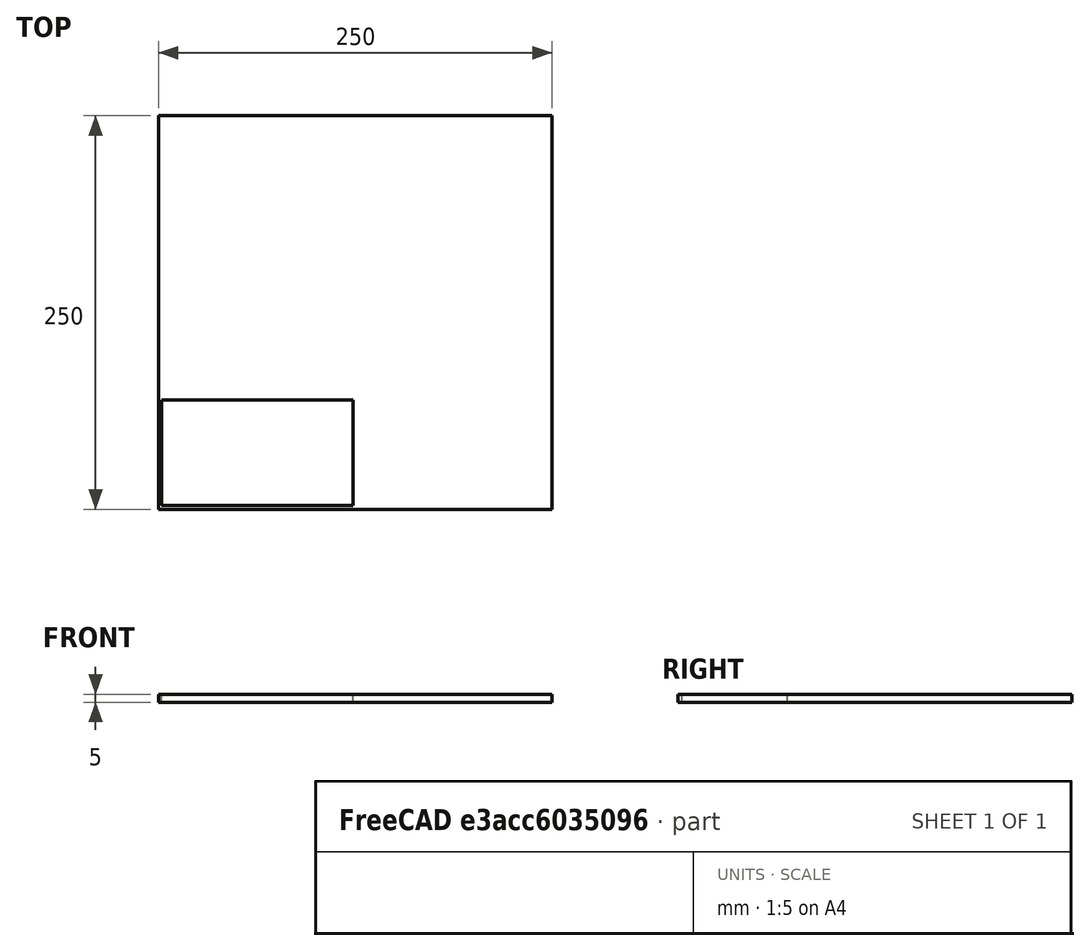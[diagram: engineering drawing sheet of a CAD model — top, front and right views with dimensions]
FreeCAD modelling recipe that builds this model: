
FCSTD DOCUMENT  (FreeCAD 0.18.4R)
Label: cnc
License: All rights reserved
LicenseURL: http://en.wikipedia.org/wiki/All_rights_reserved
objects: Path::FeaturePython×5, Part::FeaturePython×2, Part::Feature×1, App::FeaturePython×1, App::DocumentObjectGroup×1, Part::Box×1, Path::FeatureCompoundPython×1, Mesh::FeaturePython×1
note: 6 computed .brp shape members not serialized (recipe doc carries the construction recipe); baked Part::Feature solids carry a one-line shape summary decoded from their .brp

FEATURE [Part::Feature] Cut012035015003002009024006019011009006027002007011007005004011002017003001  label="drawbar001"
  Placement = pos=(163,44,-25.5) rot=(0,0,1;0rad)
  shape: bbox 119.5 x 65 x 5 mm, 31 faces (baked)
FEATURE [App::FeaturePython] SetupSheet  # Path/CAM operation (typed FeaturePython)
  ClearanceHeightExpression = OpStockZMax+SetupSheet.ClearanceHeightOffset
  ClearanceHeightOffset = 5
  FinalDepthExpression = OpFinalDepth
  HorizRapid = 15
  SafeHeightExpression = OpStockZMax+SetupSheet.SafeHeightOffset
  SafeHeightOffset = 3
  StartDepthExpression = OpStartDepth
  StepDownExpression = 0,25
  VertRapid = 15
FEATURE [Part::FeaturePython] Clone  label="Model-drawbar001"  # Draft clone (typed FeaturePython)
  AttacherType = Attacher::AttachEngine3D
  Fuse = false
  Objects = -> [Cut012035015003002009024006019011009006027002007011007005004011002017003001]
  PathResource = Model
  Placement = pos=(163,44,-25.5) rot=(0,0,1;0rad)
  Scale = (1,1,1)
FEATURE [App::DocumentObjectGroup] Model
  Group = -> [Clone]
FEATURE [Path::FeaturePython] T1__EndMill_2mm003002001  label="T1: EndMill_2mm006"  # Path/CAM operation (typed FeaturePython)
  HorizFeed = 5
  HorizRapid = 15
  SpindleDir = 0
  SpindleSpeed = 10000
  ToolNumber = 1
  VertFeed = 1.5
  VertRapid = 15
  expr: VertRapid = SetupSheet.VertRapid
  expr: HorizRapid = SetupSheet.HorizRapid
FEATURE [Path::FeaturePython] T10__EndMill_3mm  label="T10: EndMill_3mm"  # Path/CAM operation (typed FeaturePython)
  HorizFeed = 5
  HorizRapid = 15
  SpindleDir = 0
  SpindleSpeed = 10000
  ToolNumber = 10
  VertFeed = 1.5
  VertRapid = 15
  expr: HorizRapid = SetupSheet.HorizRapid
  expr: VertRapid = SetupSheet.VertRapid
FEATURE [Part::Box] Box  label="Cube"
  AttacherType = Attacher::AttachEngine3D
  Height = 5
  Length = 250
  Placement = pos=(0,0,-5) rot=(0,0,1;0rad)
  Width = 250
FEATURE [Part::FeaturePython] Stock001  # WARN: FeaturePython — macro-defined, semantics opaque (R4)
  Base = -> Model
  ExtXneg = 1
  ExtXpos = 1
  ExtYneg = 1
  ExtYpos = 1
  ExtZneg = 0
  ExtZpos = 0
  Placement = pos=(3,3.5,-5) rot=(0,0,1;0rad)
  StockType = FromBase
FEATURE [Path::FeaturePython] Profile_Edges  # Path/CAM operation (typed FeaturePython)
  Active = true
  AreaParams:
    Tolerance = 1e-07
    FitArcs = True
    Simplify = False
    CleanDistance = 0.0
    Accuracy = 0.01
    Unit = 1.0
    MinArcPoints = 4
    MaxArcPoints = 100
    ClipperScale = 10000000.0
    Fill = 0
    Coplanar = 0
    Reorient = True
    Outline = False
    Explode = False
    OpenMode = 0
    Deflection = 0.01
    SubjectFill = 0
    ClipFill = 0
    Offset = -1.475
    ExtraPass = 0
    Stepover = 0.0
    LastStepover = 0.0
    JoinType = 0
    EndType = 0
    MiterLimit = 2.0
    RoundPrecision = 0.0
    PocketMode = 0
    ToolRadius = 1.0
    PocketExtraOffset = 0.0
    PocketStepover = 0.0
    PocketLastStepover = 0.0
    FromCenter = False
    Angle = 45.0
    AngleShift = 0.0
    Shift = 0.0
    Thicken = False
    SectionCount = -1
    Stepdown = 1.0
    SectionOffset = 0.0
    SectionTolerance = 1e-06
    SectionMode = 2
    Project = False
  Base = -> [Clone]
  ClearanceHeight = 5
  Direction = 0
  FinalDepth = -5
  JoinType = 0
  MiterLimit = 0.1
  OffsetExtra = 0
  OpFinalDepth = -5
  OpStartDepth = 0
  OpStockZMax = 0
  OpStockZMin = -5
  OpToolDiameter = 2.95
  PathParams = {'orientation': 1, 'feedrate': 5.0, 'feedrate_v': 1.5, 'verbose': True, 'resume_height': 3.0, 'retraction': 5.0, 'return_end': True, 'preamble': False}
  SafeHeight = 3
  Side = 1
  StartDepth = 0
  StartPoint = (0,0,0)
  StepDown = 0.25
  ToolController = -> T10__EndMill_3mm
  UseComp = true
  UseStartPoint = false
  expr: ClearanceHeight = OpStockZMax + SetupSheet.ClearanceHeightOffset
  expr: SafeHeight = OpStockZMax + SetupSheet.SafeHeightOffset
  expr: StepDown = 0.25
  expr: FinalDepth = OpFinalDepth
  expr: StartDepth = OpStartDepth
FEATURE [Path::FeaturePython] Contour  # Path/CAM operation (typed FeaturePython)
  Active = true
  AreaParams:
    Tolerance = 1e-07
    FitArcs = True
    Simplify = False
    CleanDistance = 0.0
    Accuracy = 0.01
    Unit = 1.0
    MinArcPoints = 4
    MaxArcPoints = 100
    ClipperScale = 10000000.0
    Fill = 0
    Coplanar = 2
    Reorient = True
    Outline = False
    Explode = False
    OpenMode = 0
    Deflection = 0.01
    SubjectFill = 0
    ClipFill = 0
    Offset = 1.475
    ExtraPass = 0
    Stepover = 0.0
    LastStepover = 0.0
    JoinType = 0
    EndType = 0
    MiterLimit = 2.0
    RoundPrecision = 0.0
    PocketMode = 0
    ToolRadius = 1.0
    PocketExtraOffset = 0.0
    PocketStepover = 0.0
    PocketLastStepover = 0.0
    FromCenter = False
    Angle = 45.0
    AngleShift = 0.0
    Shift = 0.0
    Thicken = False
    SectionCount = -1
    Stepdown = 1.0
    SectionOffset = 0.0
    SectionTolerance = 1e-06
    SectionMode = 2
    Project = False
  ClearanceHeight = 5
  Direction = 0
  FinalDepth = -5
  JoinType = 0
  MiterLimit = 0.1
  OffsetExtra = 0
  OpFinalDepth = -5
  OpStartDepth = 0
  OpStockZMax = 0
  OpStockZMin = -5
  OpToolDiameter = 2.95
  PathParams = {'orientation': 1, 'feedrate': 5.0, 'feedrate_v': 1.5, 'verbose': True, 'resume_height': 3.0, 'retraction': 5.0, 'return_end': True, 'preamble': False}
  SafeHeight = 3
  Side = 0
  StartDepth = 0
  StartPoint = (0,0,0)
  StepDown = 0.25
  ToolController = -> T10__EndMill_3mm
  UseComp = true
  UseStartPoint = false
  expr: ClearanceHeight = OpStockZMax + SetupSheet.ClearanceHeightOffset
  expr: SafeHeight = OpStockZMax + SetupSheet.SafeHeightOffset
  expr: StepDown = 0.25
  expr: FinalDepth = OpFinalDepth
  expr: StartDepth = OpStartDepth
FEATURE [Path::FeatureCompoundPython] Operations  # Path/CAM operation (typed FeaturePython)
  Group = -> [Profile_Edges,Contour]
  UsePlacements = false
FEATURE [Path::FeaturePython] Job  label="drawbar-cnc"  # Path/CAM operation (typed FeaturePython)
  GeometryTolerance = 0.01
  Model = -> Model
  Operations = -> Operations
  PostProcessor = 1
  PostProcessorOutputFile = <userpath>/Data/Projects/Truck_1-14/models/Trailers/Flat/cnc/drawbar_MILL.tap
  SetupSheet = -> SetupSheet
  Stock = -> Stock001
  ToolController = -> [T1__EndMill_2mm003002001,T10__EndMill_3mm]
FEATURE [Mesh::FeaturePython] CutMaterial  # WARN: FeaturePython — macro-defined, semantics opaque (R4)
